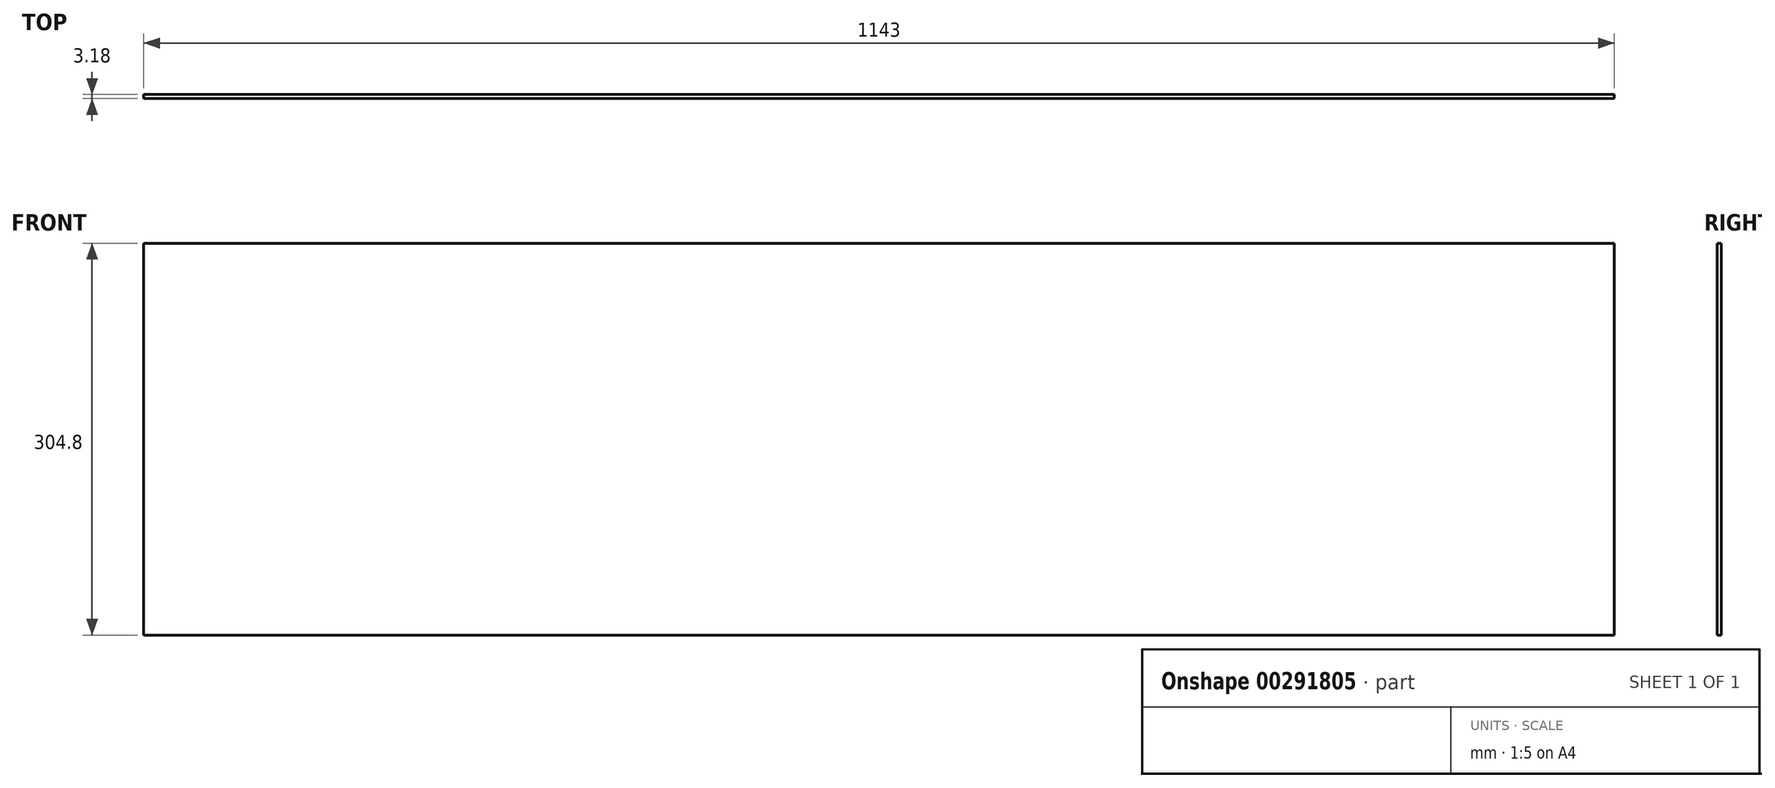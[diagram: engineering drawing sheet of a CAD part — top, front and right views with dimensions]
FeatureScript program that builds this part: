
annotation { "Feature Type Name" : "Feature", "Feature Type Description" : "" }
export const myFeature = defineFeature(function(context is Context, id is Id, definition is map)
    precondition{}
    {
        {
            var Q0;
            Q0=qCreatedBy(makeId("Front.planeOp"),FACE);
            var sketch = newSketch(context, id + "F0", { "sketchPlane" : qUnion([Q0])});
            skLineSegment(sketch, "E0.bottom", {"start": v(571.5, 152.4) * mm, "end": v(-571.5, 152.4) * mm});
            skLineSegment(sketch, "E0.top", {"start": v(571.5, -152.4) * mm, "end": v(-571.5, -152.4) * mm});
            skLineSegment(sketch, "E0.left", {"start": v(571.5, 152.4) * mm, "end": v(571.5, -152.4) * mm});
            skLineSegment(sketch, "E0.right", {"start": v(-571.5, 152.4) * mm, "end": v(-571.5, -152.4) * mm});
            skPoint(sketch, "E0.middle", {"position": v(0, 0) * mm});
            skSolve(sketch);
        }
        {
            var Q0;
            Q0 = qSketchRegion(id + "F0", true);
            extrude(context, id + "F1", {"entities" : qUnion([Q0]), "endBound" : BoundingType.SYMMETRIC, "depth" : 3.17 * mm});
        }
    });
